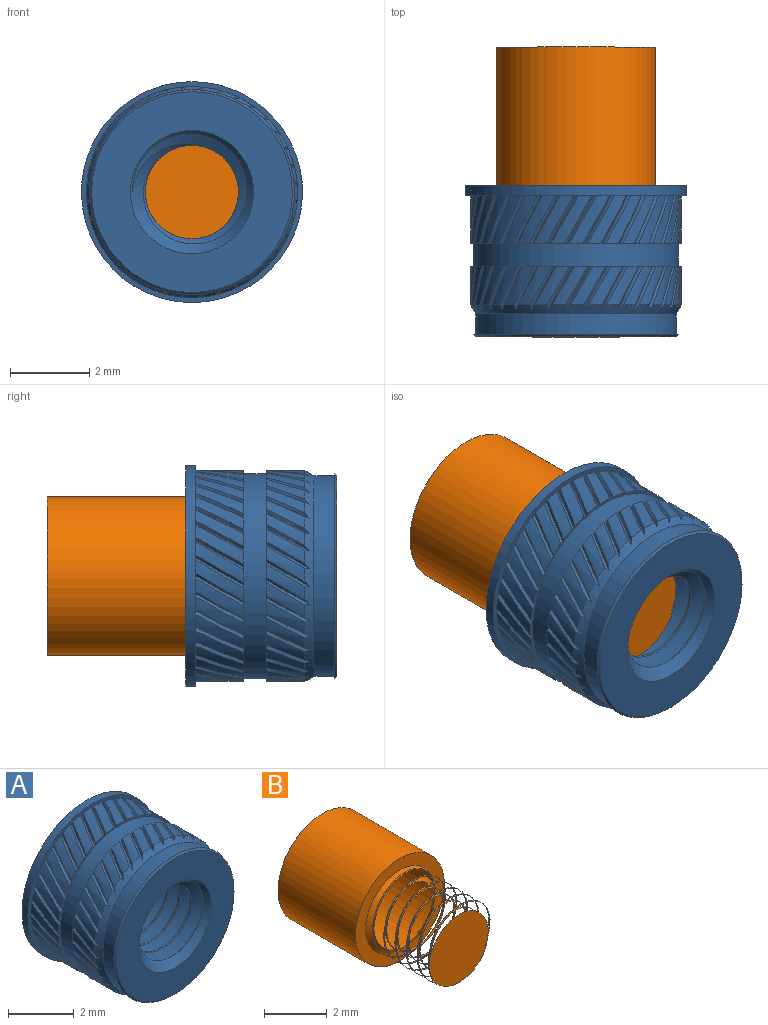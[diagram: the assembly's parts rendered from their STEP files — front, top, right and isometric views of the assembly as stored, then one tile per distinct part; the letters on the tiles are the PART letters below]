
ASSEMBLY  parts=2 mates=1
PART A: 234 faces, bbox 5.6x4.2x5.6 mm
  f0: cylinder r=2.58mm len=5.16mm, axis (0,1,0), area 9.3mm2, adj f232,f233
  f1: cone r=2.58mm half-angle=45deg, axis (0,1,0), area 1.2mm2, adj f155,f156
  f2: cone r=2.65mm half-angle=30deg, axis (0,1,0), area 3.9mm2, adj f5,f11,f12,f13,f14,f15,f16,f17
  f3: cylinder r=2.78mm len=5.56mm, axis (0,1,0), area 4.4mm2, adj f153,f154
  f4: cylinder r=2.65mm len=1.2mm, axis (0,1,0), area 0.4mm2, adj f153,f160,f163,f233
  f5: cylinder r=2.52mm len=5.05mm, axis (0,1,0), area 8.3mm2, adj f2,f155
  f6: cone r=1.55mm half-angle=45deg, axis (0,-1,0), area 2.7mm2, adj f7,f9,f156,f157,f158,f159
  f7: cone r=1.55mm half-angle=45deg, axis (0,-1,0), area 0mm2, adj f6,f9,f159
  f8: cone r=1.18mm half-angle=45deg, axis (0,1,0), area 2.7mm2, adj f9,f154,f157,f158,f159
  f9: cylinder r=1.18mm len=3.05mm, axis (0,1,0), area 2.8mm2, adj f6,f7,f8,f157,f159
  f10: cylinder r=2.65mm len=1.2mm, axis (0,1,0), area 0.4mm2, adj f153,f162,f165,f233
  f11: cylinder r=2.65mm len=0.97mm, axis (0,1,0), area 0.3mm2, adj f2,f51,f54,f232
  f12: cylinder r=2.65mm len=0.97mm, axis (0,1,0), area 0.3mm2, adj f2,f53,f55,f232
  f13: cylinder r=2.65mm len=0.97mm, axis (0,1,0), area 0.3mm2, adj f2,f115,f117,f232
  f14: cylinder r=2.65mm len=0.97mm, axis (0,1,0), area 0.3mm2, adj f2,f48,f118,f232
  f15: cylinder r=2.65mm len=0.97mm, axis (0,1,0), area 0.3mm2, adj f2,f113,f116,f232
  f16: cylinder r=2.65mm len=0.97mm, axis (0,1,0), area 0.3mm2, adj f2,f112,f114,f232
  f17: cylinder r=2.65mm len=0.97mm, axis (0,1,0), area 0.3mm2, adj f2,f107,f109,f232
  f18: cylinder r=2.65mm len=0.97mm, axis (0,1,0), area 0.3mm2, adj f2,f110,f111,f232
  f19: cylinder r=2.65mm len=0.97mm, axis (0,1,0), area 0.3mm2, adj f2,f105,f108,f232
  f20: cylinder r=2.65mm len=0.97mm, axis (0,1,0), area 0.3mm2, adj f2,f103,f106,f232
  f21: cylinder r=2.65mm len=0.97mm, axis (0,1,0), area 0.3mm2, adj f2,f101,f104,f232
  f22: cylinder r=2.65mm len=0.97mm, axis (0,1,0), area 0.3mm2, adj f2,f97,f99,f232
  f23: cylinder r=2.65mm len=0.97mm, axis (0,1,0), area 0.3mm2, adj f2,f100,f102,f232
  f24: cylinder r=2.65mm len=0.97mm, axis (0,1,0), area 0.3mm2, adj f2,f95,f98,f232
  f25: cylinder r=2.65mm len=0.97mm, axis (0,1,0), area 0.3mm2, adj f2,f94,f96,f232
  f26: cylinder r=2.65mm len=0.97mm, axis (0,1,0), area 0.3mm2, adj f2,f92,f93,f232
  f27: cylinder r=2.65mm len=0.97mm, axis (0,1,0), area 0.3mm2, adj f2,f89,f91,f232
  f28: cylinder r=2.65mm len=0.97mm, axis (0,1,0), area 0.3mm2, adj f2,f87,f90,f232
  f29: cylinder r=2.65mm len=0.97mm, axis (0,1,0), area 0.3mm2, adj f2,f85,f88,f232
  f30: cylinder r=2.65mm len=0.97mm, axis (0,1,0), area 0.3mm2, adj f2,f83,f86,f232
  f31: cylinder r=2.65mm len=0.97mm, axis (0,1,0), area 0.3mm2, adj f2,f82,f84,f232
  f32: cylinder r=2.65mm len=0.97mm, axis (0,1,0), area 0.3mm2, adj f2,f79,f81,f232
  f33: cylinder r=2.65mm len=0.97mm, axis (0,1,0), area 0.3mm2, adj f2,f77,f80,f232
  f34: cylinder r=2.65mm len=0.97mm, axis (0,1,0), area 0.3mm2, adj f2,f76,f78,f232
  f35: cylinder r=2.65mm len=0.97mm, axis (0,1,0), area 0.3mm2, adj f2,f71,f73,f232
  f36: cylinder r=2.65mm len=0.97mm, axis (0,1,0), area 0.3mm2, adj f2,f74,f75,f232
  f37: cylinder r=2.65mm len=0.97mm, axis (0,1,0), area 0.3mm2, adj f2,f69,f72,f232
  f38: cylinder r=2.65mm len=0.97mm, axis (0,1,0), area 0.3mm2, adj f2,f67,f70,f232
  f39: cylinder r=2.65mm len=0.97mm, axis (0,1,0), area 0.3mm2, adj f2,f65,f68,f232
  f40: cylinder r=2.65mm len=0.97mm, axis (0,1,0), area 0.3mm2, adj f2,f61,f63,f232
  f41: cylinder r=2.65mm len=0.97mm, axis (0,1,0), area 0.3mm2, adj f2,f64,f66,f232
  f42: cylinder r=2.65mm len=0.97mm, axis (0,1,0), area 0.3mm2, adj f2,f59,f62,f232
  f43: cylinder r=2.65mm len=0.97mm, axis (0,1,0), area 0.3mm2, adj f2,f56,f57,f232
  f44: cylinder r=2.65mm len=0.97mm, axis (0,1,0), area 0.3mm2, adj f2,f58,f60,f232
  f45: cylinder r=2.65mm len=0.97mm, axis (0,1,0), area 0.3mm2, adj f2,f49,f52,f232
  f46: cylinder r=2.65mm len=0.97mm, axis (0,1,0), area 0.3mm2, adj f2,f47,f50,f232
  f47: bspline ~1.08x0.57mm, area 0.1mm2, adj f2,f46,f48,f232
  f48: bspline ~1.21x0.69mm, area 0.1mm2, adj f2,f14,f47,f232
  f49: bspline ~1.08x0.63mm, area 0.1mm2, adj f2,f45,f50,f232
  f50: bspline ~1.21x0.74mm, area 0.1mm2, adj f2,f46,f49,f232
  f51: bspline ~1.08x0.67mm, area 0.1mm2, adj f2,f11,f52,f232
  f52: bspline ~1.21x0.76mm, area 0.1mm2, adj f2,f45,f51,f232
  f53: bspline ~1.08x0.69mm, area 0.1mm2, adj f2,f12,f54,f232
  f54: bspline ~1.21x0.76mm, area 0.1mm2, adj f2,f11,f53,f232
  f55: bspline ~1.31x0.79mm, area 0.1mm2, adj f2,f12,f56,f232
  f56: bspline ~1.31x0.81mm, area 0.1mm2, adj f2,f43,f55,f232
  f57: bspline ~1.31x0.74mm, area 0.1mm2, adj f2,f43,f58,f232
  f58: bspline ~1.31x0.78mm, area 0.1mm2, adj f2,f44,f57,f232
  f59: bspline ~1.21x0.67mm, area 0.1mm2, adj f2,f42,f60,f232
  f60: bspline ~1.21x0.62mm, area 0.1mm2, adj f2,f44,f59,f232
  f61: bspline ~1.21x0.6mm, area 0.1mm2, adj f2,f40,f62,f232
  f62: bspline ~1.21x0.54mm, area 0.1mm2, adj f2,f42,f61,f232
  f63: bspline ~1.31x0.67mm, area 0.1mm2, adj f2,f40,f64,f232
  f64: bspline ~1.31x0.6mm, area 0.1mm2, adj f2,f41,f63,f232
  f65: bspline ~1.08x0.57mm, area 0.1mm2, adj f2,f39,f66,f232
  f66: bspline ~1.21x0.69mm, area 0.1mm2, adj f2,f41,f65,f232
  f67: bspline ~1.08x0.63mm, area 0.1mm2, adj f2,f38,f68,f232
  f68: bspline ~1.21x0.74mm, area 0.1mm2, adj f2,f39,f67,f232
  f69: bspline ~1.08x0.67mm, area 0.1mm2, adj f2,f37,f70,f232
  f70: bspline ~1.21x0.76mm, area 0.1mm2, adj f2,f38,f69,f232
  f71: bspline ~1.08x0.69mm, area 0.1mm2, adj f2,f35,f72,f232
  f72: bspline ~1.21x0.76mm, area 0.1mm2, adj f2,f37,f71,f232
  f73: bspline ~1.31x0.79mm, area 0.1mm2, adj f2,f35,f74,f232
  f74: bspline ~1.31x0.81mm, area 0.1mm2, adj f2,f36,f73,f232
  f75: bspline ~1.31x0.74mm, area 0.1mm2, adj f2,f36,f76,f232
  f76: bspline ~1.31x0.78mm, area 0.1mm2, adj f2,f34,f75,f232
  f77: bspline ~1.21x0.67mm, area 0.1mm2, adj f2,f33,f78,f232
  f78: bspline ~1.21x0.62mm, area 0.1mm2, adj f2,f34,f77,f232
  f79: bspline ~1.21x0.6mm, area 0.1mm2, adj f2,f32,f80,f232
  f80: bspline ~1.21x0.54mm, area 0.1mm2, adj f2,f33,f79,f232
  f81: bspline ~1.31x0.67mm, area 0.1mm2, adj f2,f32,f82,f232
  f82: bspline ~1.31x0.6mm, area 0.1mm2, adj f2,f31,f81,f232
  f83: bspline ~1.08x0.57mm, area 0.1mm2, adj f2,f30,f84,f232
  f84: bspline ~1.21x0.69mm, area 0.1mm2, adj f2,f31,f83,f232
  f85: bspline ~1.08x0.63mm, area 0.1mm2, adj f2,f29,f86,f232
  f86: bspline ~1.21x0.74mm, area 0.1mm2, adj f2,f30,f85,f232
  f87: bspline ~1.08x0.67mm, area 0.1mm2, adj f2,f28,f88,f232
  f88: bspline ~1.21x0.76mm, area 0.1mm2, adj f2,f29,f87,f232
  f89: bspline ~1.08x0.69mm, area 0.1mm2, adj f2,f27,f90,f232
  f90: bspline ~1.21x0.76mm, area 0.1mm2, adj f2,f28,f89,f232
  f91: bspline ~1.31x0.79mm, area 0.1mm2, adj f2,f27,f92,f232
  f92: bspline ~1.31x0.81mm, area 0.1mm2, adj f2,f26,f91,f232
  f93: bspline ~1.31x0.74mm, area 0.1mm2, adj f2,f26,f94,f232
  f94: bspline ~1.31x0.78mm, area 0.1mm2, adj f2,f25,f93,f232
  f95: bspline ~1.21x0.67mm, area 0.1mm2, adj f2,f24,f96,f232
  f96: bspline ~1.21x0.62mm, area 0.1mm2, adj f2,f25,f95,f232
  f97: bspline ~1.21x0.6mm, area 0.1mm2, adj f2,f22,f98,f232
  f98: bspline ~1.21x0.54mm, area 0.1mm2, adj f2,f24,f97,f232
  f99: bspline ~1.31x0.67mm, area 0.1mm2, adj f2,f22,f100,f232
  f100: bspline ~1.31x0.6mm, area 0.1mm2, adj f2,f23,f99,f232
  f101: bspline ~1.08x0.57mm, area 0.1mm2, adj f2,f21,f102,f232
  f102: bspline ~1.21x0.69mm, area 0.1mm2, adj f2,f23,f101,f232
  f103: bspline ~1.08x0.63mm, area 0.1mm2, adj f2,f20,f104,f232
  f104: bspline ~1.21x0.74mm, area 0.1mm2, adj f2,f21,f103,f232
  f105: bspline ~1.08x0.67mm, area 0.1mm2, adj f2,f19,f106,f232
  f106: bspline ~1.21x0.76mm, area 0.1mm2, adj f2,f20,f105,f232
  f107: bspline ~1.08x0.69mm, area 0.1mm2, adj f2,f17,f108,f232
  f108: bspline ~1.21x0.76mm, area 0.1mm2, adj f2,f19,f107,f232
  f109: bspline ~1.31x0.79mm, area 0.1mm2, adj f2,f17,f110,f232
  f110: bspline ~1.31x0.81mm, area 0.1mm2, adj f2,f18,f109,f232
  f111: bspline ~1.31x0.74mm, area 0.1mm2, adj f2,f18,f112,f232
  f112: bspline ~1.31x0.78mm, area 0.1mm2, adj f2,f16,f111,f232
  f113: bspline ~1.21x0.67mm, area 0.1mm2, adj f2,f15,f114,f232
  f114: bspline ~1.21x0.62mm, area 0.1mm2, adj f2,f16,f113,f232
  f115: bspline ~1.21x0.6mm, area 0.1mm2, adj f2,f13,f116,f232
  f116: bspline ~1.21x0.54mm, area 0.1mm2, adj f2,f15,f115,f232
  f117: bspline ~1.31x0.67mm, area 0.1mm2, adj f2,f13,f118,f232
  f118: bspline ~1.31x0.6mm, area 0.1mm2, adj f2,f14,f117,f232
  f119: cylinder r=2.65mm len=1.2mm, axis (0,1,0), area 0.4mm2, adj f153,f228,f231,f233
  f120: cylinder r=2.65mm len=1.2mm, axis (0,1,0), area 0.4mm2, adj f153,f161,f230,f233
  f121: cylinder r=2.65mm len=1.2mm, axis (0,1,0), area 0.4mm2, adj f153,f226,f229,f233
  f122: cylinder r=2.65mm len=1.2mm, axis (0,1,0), area 0.4mm2, adj f153,f224,f227,f233
  f123: cylinder r=2.65mm len=1.2mm, axis (0,1,0), area 0.4mm2, adj f153,f220,f223,f233
  f124: cylinder r=2.65mm len=1.2mm, axis (0,1,0), area 0.4mm2, adj f153,f222,f225,f233
  f125: cylinder r=2.65mm len=1.2mm, axis (0,1,0), area 0.4mm2, adj f153,f218,f221,f233
  f126: cylinder r=2.65mm len=1.2mm, axis (0,1,0), area 0.4mm2, adj f153,f216,f219,f233
  f127: cylinder r=2.65mm len=1.2mm, axis (0,1,0), area 0.4mm2, adj f153,f214,f217,f233
  f128: cylinder r=2.65mm len=1.2mm, axis (0,1,0), area 0.4mm2, adj f153,f210,f213,f233
  f129: cylinder r=2.65mm len=1.2mm, axis (0,1,0), area 0.4mm2, adj f153,f212,f215,f233
  f130: cylinder r=2.65mm len=1.2mm, axis (0,1,0), area 0.4mm2, adj f153,f208,f211,f233
  f131: cylinder r=2.65mm len=1.2mm, axis (0,1,0), area 0.4mm2, adj f153,f206,f209,f233
  f132: cylinder r=2.65mm len=1.2mm, axis (0,1,0), area 0.4mm2, adj f153,f204,f207,f233
  f133: cylinder r=2.65mm len=1.2mm, axis (0,1,0), area 0.4mm2, adj f153,f202,f205,f233
  f134: cylinder r=2.65mm len=1.2mm, axis (0,1,0), area 0.4mm2, adj f153,f200,f203,f233
  f135: cylinder r=2.65mm len=1.2mm, axis (0,1,0), area 0.4mm2, adj f153,f198,f201,f233
  f136: cylinder r=2.65mm len=1.2mm, axis (0,1,0), area 0.4mm2, adj f153,f196,f199,f233
  f137: cylinder r=2.65mm len=1.2mm, axis (0,1,0), area 0.4mm2, adj f153,f194,f197,f233
  f138: cylinder r=2.65mm len=1.2mm, axis (0,1,0), area 0.4mm2, adj f153,f192,f195,f233
  f139: cylinder r=2.65mm len=1.2mm, axis (0,1,0), area 0.4mm2, adj f153,f190,f193,f233
  f140: cylinder r=2.65mm len=1.2mm, axis (0,1,0), area 0.4mm2, adj f153,f188,f191,f233
  f141: cylinder r=2.65mm len=1.2mm, axis (0,1,0), area 0.4mm2, adj f153,f184,f187,f233
  f142: cylinder r=2.65mm len=1.2mm, axis (0,1,0), area 0.4mm2, adj f153,f186,f189,f233
  f143: cylinder r=2.65mm len=1.2mm, axis (0,1,0), area 0.4mm2, adj f153,f182,f185,f233
  f144: cylinder r=2.65mm len=1.2mm, axis (0,1,0), area 0.4mm2, adj f153,f180,f183,f233
  f145: cylinder r=2.65mm len=1.2mm, axis (0,1,0), area 0.4mm2, adj f153,f178,f181,f233
  f146: cylinder r=2.65mm len=1.2mm, axis (0,1,0), area 0.4mm2, adj f153,f174,f177,f233
  f147: cylinder r=2.65mm len=1.2mm, axis (0,1,0), area 0.4mm2, adj f153,f176,f179,f233
  f148: cylinder r=2.65mm len=1.2mm, axis (0,1,0), area 0.4mm2, adj f153,f172,f175,f233
  f149: cylinder r=2.65mm len=1.2mm, axis (0,1,0), area 0.4mm2, adj f153,f168,f171,f233
  f150: cylinder r=2.65mm len=1.2mm, axis (0,1,0), area 0.4mm2, adj f153,f170,f173,f233
  f151: cylinder r=2.65mm len=1.2mm, axis (0,1,0), area 0.4mm2, adj f153,f166,f169,f233
  f152: cylinder r=2.65mm len=1.2mm, axis (0,1,0), area 0.4mm2, adj f153,f164,f167,f233
  f153: plane 5.56x5.56mm, normal (0,-1,0), area 2.3mm2, adj f3,f4,f10,f119,f120,f121,f122,f123
  f154: plane 5.56x5.56mm, normal (0,1,0), area 16.7mm2, adj f3,f8
  f155: plane 5.16x5.16mm, normal (0,1,0), area 0.9mm2, adj f1,f5
  f156: plane 5.05x5.05mm, normal (0,-1,0), area 12.5mm2, adj f1,f6
  f157: bspline ~4.04x3.46mm, area 21.4mm2, adj f6,f8,f9,f158
  f158: cylinder r=1.5mm len=3.7mm, axis (0,-1,0), area 6mm2, adj f6,f8,f157,f159
  f159: bspline ~3.95x3.46mm, area 21.4mm2, adj f6,f7,f8,f9,f158
  f160: bspline ~1.31x0.79mm, area 0.1mm2, adj f4,f153,f161,f233
  f161: bspline ~1.31x0.81mm, area 0.1mm2, adj f120,f153,f160,f233
  f162: bspline ~1.31x0.81mm, area 0.1mm2, adj f10,f153,f163,f233
  f163: bspline ~1.31x0.81mm, area 0.1mm2, adj f4,f153,f162,f233
  f164: bspline ~1.31x0.81mm, area 0.1mm2, adj f152,f153,f165,f233
  f165: bspline ~1.31x0.78mm, area 0.1mm2, adj f10,f153,f164,f233
  f166: bspline ~1.2x0.71mm, area 0.1mm2, adj f151,f153,f167,f233
  f167: bspline ~1.31x0.73mm, area 0.1mm2, adj f152,f153,f166,f233
  f168: bspline ~1.31x0.72mm, area 0.1mm2, adj f149,f153,f169,f233
  f169: bspline ~1.31x0.66mm, area 0.1mm2, adj f151,f153,f168,f233
  f170: bspline ~1.31x0.64mm, area 0.1mm2, adj f150,f153,f171,f233
  f171: bspline ~1.31x0.58mm, area 0.1mm2, adj f149,f153,f170,f233
  f172: bspline ~1.2x0.56mm, area 0.1mm2, adj f148,f153,f173,f233
  f173: bspline ~1.31x0.67mm, area 0.1mm2, adj f150,f153,f172,f233
  f174: bspline ~1.2x0.64mm, area 0.1mm2, adj f146,f153,f175,f233
  f175: bspline ~1.31x0.74mm, area 0.1mm2, adj f148,f153,f174,f233
  f176: bspline ~1.31x0.75mm, area 0.1mm2, adj f147,f153,f177,f233
  f177: bspline ~1.31x0.79mm, area 0.1mm2, adj f146,f153,f176,f233
  f178: bspline ~1.31x0.79mm, area 0.1mm2, adj f145,f153,f179,f233
  f179: bspline ~1.31x0.81mm, area 0.1mm2, adj f147,f153,f178,f233
  f180: bspline ~1.31x0.81mm, area 0.1mm2, adj f144,f153,f181,f233
  f181: bspline ~1.31x0.81mm, area 0.1mm2, adj f145,f153,f180,f233
  f182: bspline ~1.31x0.81mm, area 0.1mm2, adj f143,f153,f183,f233
  f183: bspline ~1.31x0.78mm, area 0.1mm2, adj f144,f153,f182,f233
  f184: bspline ~1.2x0.71mm, area 0.1mm2, adj f141,f153,f185,f233
  f185: bspline ~1.31x0.73mm, area 0.1mm2, adj f143,f153,f184,f233
  f186: bspline ~1.31x0.72mm, area 0.1mm2, adj f142,f153,f187,f233
  f187: bspline ~1.31x0.66mm, area 0.1mm2, adj f141,f153,f186,f233
  f188: bspline ~1.31x0.64mm, area 0.1mm2, adj f140,f153,f189,f233
  f189: bspline ~1.31x0.58mm, area 0.1mm2, adj f142,f153,f188,f233
  f190: bspline ~1.2x0.56mm, area 0.1mm2, adj f139,f153,f191,f233
  f191: bspline ~1.31x0.67mm, area 0.1mm2, adj f140,f153,f190,f233
  f192: bspline ~1.2x0.64mm, area 0.1mm2, adj f138,f153,f193,f233
  f193: bspline ~1.31x0.74mm, area 0.1mm2, adj f139,f153,f192,f233
  f194: bspline ~1.31x0.75mm, area 0.1mm2, adj f137,f153,f195,f233
  f195: bspline ~1.31x0.79mm, area 0.1mm2, adj f138,f153,f194,f233
  f196: bspline ~1.31x0.79mm, area 0.1mm2, adj f136,f153,f197,f233
  f197: bspline ~1.31x0.81mm, area 0.1mm2, adj f137,f153,f196,f233
  f198: bspline ~1.31x0.81mm, area 0.1mm2, adj f135,f153,f199,f233
  f199: bspline ~1.31x0.81mm, area 0.1mm2, adj f136,f153,f198,f233
  f200: bspline ~1.31x0.81mm, area 0.1mm2, adj f134,f153,f201,f233
  f201: bspline ~1.31x0.78mm, area 0.1mm2, adj f135,f153,f200,f233
  f202: bspline ~1.2x0.71mm, area 0.1mm2, adj f133,f153,f203,f233
  f203: bspline ~1.31x0.73mm, area 0.1mm2, adj f134,f153,f202,f233
  f204: bspline ~1.31x0.72mm, area 0.1mm2, adj f132,f153,f205,f233
  f205: bspline ~1.31x0.66mm, area 0.1mm2, adj f133,f153,f204,f233
  f206: bspline ~1.31x0.64mm, area 0.1mm2, adj f131,f153,f207,f233
  f207: bspline ~1.31x0.58mm, area 0.1mm2, adj f132,f153,f206,f233
  f208: bspline ~1.2x0.56mm, area 0.1mm2, adj f130,f153,f209,f233
  f209: bspline ~1.31x0.67mm, area 0.1mm2, adj f131,f153,f208,f233
  f210: bspline ~1.2x0.64mm, area 0.1mm2, adj f128,f153,f211,f233
  f211: bspline ~1.31x0.74mm, area 0.1mm2, adj f130,f153,f210,f233
  f212: bspline ~1.31x0.75mm, area 0.1mm2, adj f129,f153,f213,f233
  f213: bspline ~1.31x0.79mm, area 0.1mm2, adj f128,f153,f212,f233
  f214: bspline ~1.31x0.79mm, area 0.1mm2, adj f127,f153,f215,f233
  f215: bspline ~1.31x0.81mm, area 0.1mm2, adj f129,f153,f214,f233
  f216: bspline ~1.31x0.81mm, area 0.1mm2, adj f126,f153,f217,f233
  f217: bspline ~1.31x0.81mm, area 0.1mm2, adj f127,f153,f216,f233
  f218: bspline ~1.31x0.81mm, area 0.1mm2, adj f125,f153,f219,f233
  f219: bspline ~1.31x0.78mm, area 0.1mm2, adj f126,f153,f218,f233
  f220: bspline ~1.2x0.71mm, area 0.1mm2, adj f123,f153,f221,f233
  f221: bspline ~1.31x0.73mm, area 0.1mm2, adj f125,f153,f220,f233
  f222: bspline ~1.31x0.72mm, area 0.1mm2, adj f124,f153,f223,f233
  f223: bspline ~1.31x0.66mm, area 0.1mm2, adj f123,f153,f222,f233
  f224: bspline ~1.31x0.64mm, area 0.1mm2, adj f122,f153,f225,f233
  f225: bspline ~1.31x0.58mm, area 0.1mm2, adj f124,f153,f224,f233
  f226: bspline ~1.2x0.56mm, area 0.1mm2, adj f121,f153,f227,f233
  f227: bspline ~1.31x0.67mm, area 0.1mm2, adj f122,f153,f226,f233
  f228: bspline ~1.2x0.64mm, area 0.1mm2, adj f119,f153,f229,f233
  f229: bspline ~1.31x0.74mm, area 0.1mm2, adj f121,f153,f228,f233
  f230: bspline ~1.31x0.75mm, area 0.1mm2, adj f120,f153,f231,f233
  f231: bspline ~1.31x0.79mm, area 0.1mm2, adj f119,f153,f230,f233
  f232: plane 5.31x5.31mm, normal (0,1,0), area 1.1mm2, adj f0,f11,f12,f13,f14,f15,f16,f17
  f233: plane 5.31x5.31mm, normal (0,-1,0), area 1.1mm2, adj f0,f4,f10,f119,f120,f121,f122,f123
PART B: 8 faces, bbox 4x6.3x4 mm
  f0: cylinder r=2mm len=4mm, axis (0,-1,0), area 43.9mm2, adj f1,f2
  f1: plane 4x4mm, normal (0,1,0), area 12.6mm2, adj f0
  f2: plane 4x4mm, normal (0,-1,0), area 5.1mm2, adj f0,f5
  f3: cylinder r=1.17mm len=2.43mm, axis (0,1,0), area 2.6mm2, adj f5,f6,f7
  f4: cylinder r=1.49mm len=2.98mm, axis (0,-1,0), area 2.7mm2, adj f5,f7
  f5: cone r=1.17mm half-angle=45deg, axis (0,1,0), area 2.8mm2, adj f2,f3,f4,f6
  f6: cone r=1.17mm half-angle=45deg, axis (0,1,0), area 0mm2, adj f3,f5
  f7: plane 2.66x2.65mm, normal (0,-1,0), area 5.5mm2, adj f3,f4
PLACE A at identity
PLACE B t=(0,-0.01,0)mm
MATE fastened A.f0 <-> B.f0  axis (0,1,0) through (0,0,0)mm
